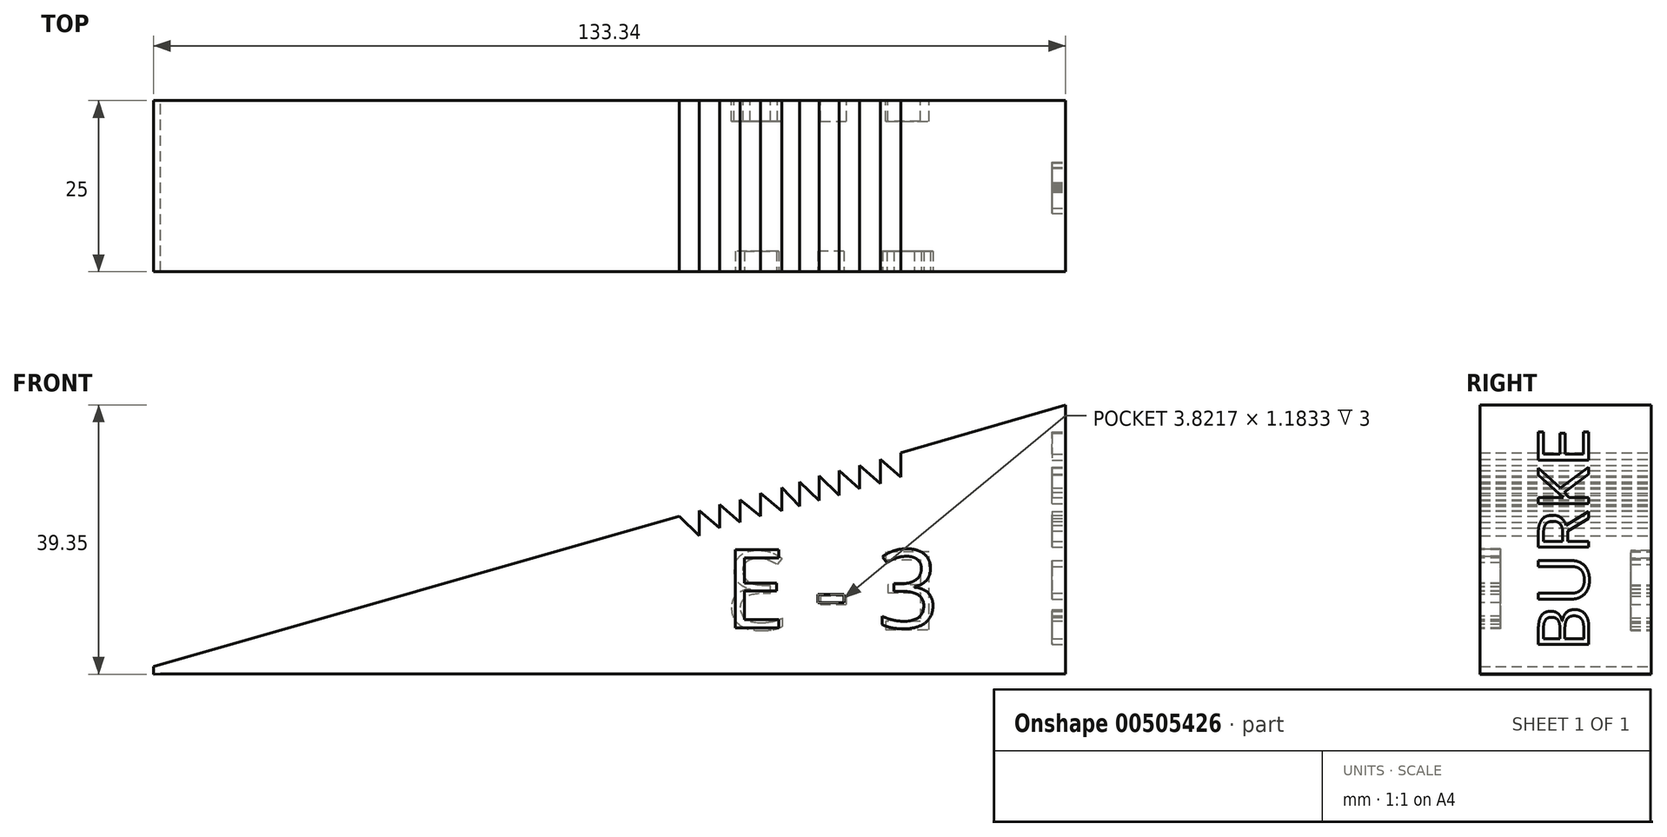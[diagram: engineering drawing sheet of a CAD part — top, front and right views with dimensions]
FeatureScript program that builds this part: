
annotation { "Feature Type Name" : "Feature", "Feature Type Description" : "" }
export const myFeature = defineFeature(function(context is Context, id is Id, definition is map)
    precondition{}
    {
        {
            var Q0;
            Q0=qCreatedBy(makeId("Front.planeOp"),FACE);
            var sketch = newSketch(context, id + "F0", { "sketchPlane" : qUnion([Q0])});
            skLineSegment(sketch, "E0", {"start": v(-57.96, -21.36) * mm, "end": v(74.33, -21.36) * mm});
            skLineSegment(sketch, "E1", {"start": v(74.33, -21.36) * mm, "end": v(74.33, 17.97) * mm});
            skLineSegment(sketch, "E2", {"start": v(74.33, 17.97) * mm, "end": v(50.24, 11) * mm});
            skLineSegment(sketch, "E3", {"start": v(50.24, 11) * mm, "end": v(50.24, 7.43) * mm});
            skLineSegment(sketch, "E4", {"start": v(50.24, 7.43) * mm, "end": v(47.23, 10.07) * mm});
            skLineSegment(sketch, "E5", {"start": v(47.23, 10.07) * mm, "end": v(47.23, 6.5) * mm});
            skLineSegment(sketch, "E6", {"start": v(47.23, 6.5) * mm, "end": v(44.22, 9.13) * mm});
            skLineSegment(sketch, "E7", {"start": v(44.22, 9.13) * mm, "end": v(44.22, 5.74) * mm});
            skLineSegment(sketch, "E8", {"start": v(44.22, 5.74) * mm, "end": v(41.2, 8.37) * mm});
            skLineSegment(sketch, "E9", {"start": v(41.2, 8.37) * mm, "end": v(41.2, 4.8) * mm});
            skLineSegment(sketch, "E10", {"start": v(41.2, 4.8) * mm, "end": v(38.28, 7.6) * mm});
            skLineSegment(sketch, "E11", {"start": v(38.28, 7.6) * mm, "end": v(38.28, 4) * mm});
            skLineSegment(sketch, "E12", {"start": v(38.28, 4) * mm, "end": v(35.43, 6.76) * mm});
            skLineSegment(sketch, "E13", {"start": v(35.43, 6.76) * mm, "end": v(35.43, 3.16) * mm});
            skLineSegment(sketch, "E14", {"start": v(35.43, 3.16) * mm, "end": v(32.83, 5.92) * mm});
            skLineSegment(sketch, "E15", {"start": v(32.83, 5.92) * mm, "end": v(32.83, 2.49) * mm});
            skLineSegment(sketch, "E16", {"start": v(32.83, 2.49) * mm, "end": v(29.73, 5.08) * mm});
            skLineSegment(sketch, "E17", {"start": v(29.73, 5.08) * mm, "end": v(29.73, 1.73) * mm});
            skLineSegment(sketch, "E18", {"start": v(29.73, 1.73) * mm, "end": v(26.71, 4.16) * mm});
            skLineSegment(sketch, "E19", {"start": v(26.71, 4.16) * mm, "end": v(26.71, 0.8) * mm});
            skLineSegment(sketch, "E20", {"start": v(26.71, 0.8) * mm, "end": v(23.78, 3.4) * mm});
            skLineSegment(sketch, "E21", {"start": v(23.78, 3.4) * mm, "end": v(23.78, 0) * mm});
            skLineSegment(sketch, "E22", {"start": v(23.78, 0) * mm, "end": v(20.76, 2.57) * mm});
            skLineSegment(sketch, "E23", {"start": v(20.76, 2.57) * mm, "end": v(20.76, -1.12) * mm});
            skLineSegment(sketch, "E24", {"start": v(20.76, -1.12) * mm, "end": v(17.83, 1.73) * mm});
            skLineSegment(sketch, "E25", {"start": v(17.83, 1.73) * mm, "end": v(-59.01, -20.26) * mm});
            skLineSegment(sketch, "E26", {"start": v(-59.01, -20.26) * mm, "end": v(-59.01, -21.38) * mm});
            skLineSegment(sketch, "E27", {"start": v(-59.01, -21.38) * mm, "end": v(-57.96, -21.36) * mm});
            skSolve(sketch);
        }
        {
            var Q0;
            Q0=makeQuery(id+"F0.imprint","IMPRINT",FACE,{"disambiguationData":[TD([[makeQuery(id+"F0.imprint","IMPRINT",EDGE,{"derivedFrom":sQuery(id+"F0.wireOp",EDGE,"E0")}),1.0]])]});
            extrude(context, id + "F1", {"entities" : qUnion([Q0]), "depth" : 25 * mm});
        }
        {
            var Q0;
            Q0=makeQuery(id+"F1.opExtrude","CAP_FACE",FACE,{"disambiguationData":[OSD([sQuery(id+"F0.wireOp",EDGE,"E0"),sQuery(id+"F0.wireOp",EDGE,"E1"),sQuery(id+"F0.wireOp",EDGE,"E2"),sQuery(id+"F0.wireOp",EDGE,"E3"),sQuery(id+"F0.wireOp",EDGE,"E4"),sQuery(id+"F0.wireOp",EDGE,"E5"),sQuery(id+"F0.wireOp",EDGE,"E6"),sQuery(id+"F0.wireOp",EDGE,"E7"),sQuery(id+"F0.wireOp",EDGE,"E8"),sQuery(id+"F0.wireOp",EDGE,"E9"),sQuery(id+"F0.wireOp",EDGE,"E10"),sQuery(id+"F0.wireOp",EDGE,"E11"),sQuery(id+"F0.wireOp",EDGE,"E12"),sQuery(id+"F0.wireOp",EDGE,"E13"),sQuery(id+"F0.wireOp",EDGE,"E14"),sQuery(id+"F0.wireOp",EDGE,"E15"),sQuery(id+"F0.wireOp",EDGE,"E16"),sQuery(id+"F0.wireOp",EDGE,"E17"),sQuery(id+"F0.wireOp",EDGE,"E18"),sQuery(id+"F0.wireOp",EDGE,"E19"),sQuery(id+"F0.wireOp",EDGE,"E20"),sQuery(id+"F0.wireOp",EDGE,"E21"),sQuery(id+"F0.wireOp",EDGE,"E22"),sQuery(id+"F0.wireOp",EDGE,"E23"),sQuery(id+"F0.wireOp",EDGE,"E24"),sQuery(id+"F0.wireOp",EDGE,"E25"),sQuery(id+"F0.wireOp",EDGE,"E26"),sQuery(id+"F0.wireOp",EDGE,"E27")])],"isStart":false});
            var sketch = newSketch(context, id + "F2", { "sketchPlane" : qUnion([Q0])});
            skText(sketch, "E28", { "text": "E - 3", "fontName": "OpenSans-Regular.ttf"});
            const initialGuessF2  = {"E28": [0.02446, -0.01458, 1, 0, 0.01148]};
            skSetInitialGuess(sketch, initialGuessF2);
            skSolve(sketch);
        }
        {
            var Q0;
            Q0=makeQuery(id+"F1.opExtrude","CAP_FACE",FACE,{"disambiguationData":[OSD([sQuery(id+"F0.wireOp",EDGE,"E0"),sQuery(id+"F0.wireOp",EDGE,"E1"),sQuery(id+"F0.wireOp",EDGE,"E2"),sQuery(id+"F0.wireOp",EDGE,"E3"),sQuery(id+"F0.wireOp",EDGE,"E4"),sQuery(id+"F0.wireOp",EDGE,"E5"),sQuery(id+"F0.wireOp",EDGE,"E6"),sQuery(id+"F0.wireOp",EDGE,"E7"),sQuery(id+"F0.wireOp",EDGE,"E8"),sQuery(id+"F0.wireOp",EDGE,"E9"),sQuery(id+"F0.wireOp",EDGE,"E10"),sQuery(id+"F0.wireOp",EDGE,"E11"),sQuery(id+"F0.wireOp",EDGE,"E12"),sQuery(id+"F0.wireOp",EDGE,"E13"),sQuery(id+"F0.wireOp",EDGE,"E14"),sQuery(id+"F0.wireOp",EDGE,"E15"),sQuery(id+"F0.wireOp",EDGE,"E16"),sQuery(id+"F0.wireOp",EDGE,"E17"),sQuery(id+"F0.wireOp",EDGE,"E18"),sQuery(id+"F0.wireOp",EDGE,"E19"),sQuery(id+"F0.wireOp",EDGE,"E20"),sQuery(id+"F0.wireOp",EDGE,"E21"),sQuery(id+"F0.wireOp",EDGE,"E22"),sQuery(id+"F0.wireOp",EDGE,"E23"),sQuery(id+"F0.wireOp",EDGE,"E24"),sQuery(id+"F0.wireOp",EDGE,"E25"),sQuery(id+"F0.wireOp",EDGE,"E26"),sQuery(id+"F0.wireOp",EDGE,"E27")])],"isStart":true});
            var sketch = newSketch(context, id + "F3", { "sketchPlane" : qUnion([Q0])});
            skText(sketch, "E29", { "text": "E - 3", "fontName": "OpenSans-Regular.ttf"});
            const initialGuessF3  = {"E29": [-0.05595, -0.01485, 1, 0, 0.01148]};
            skSetInitialGuess(sketch, initialGuessF3);
            skSolve(sketch);
        }
        {
            var Q0;
            Q0=qSketchRegion(id+"F2",true);
            extrude(context, id + "F4", {"entities" : qUnion([Q0]), "operationType" : NewBodyOperationType.REMOVE, "oppositeDirection" : true, "depth" : 3 * mm});
        }
        {
            var Q0;
            Q0=qSketchRegion(id+"F3",true);
            extrude(context, id + "F5", {"entities" : qUnion([Q0]), "operationType" : NewBodyOperationType.REMOVE, "oppositeDirection" : true, "depth" : 3 * mm});
        }
        {
            var Q0;
            Q0=makeQuery(id+"F1.opExtrude","SWEPT_FACE",FACE,{"disambiguationData":[OSD([sQuery(id+"F0.wireOp",EDGE,"E1")])]});
            var sketch = newSketch(context, id + "F6", { "sketchPlane" : qUnion([Q0])});
            skText(sketch, "E30", { "text": "BURKE", "fontName": "OpenSans-Regular.ttf"});
            const initialGuessF6  = {"E30": [-0.00911, -0.01804, 0, 1, 0.00744]};
            skSetInitialGuess(sketch, initialGuessF6);
            skSolve(sketch);
        }
        {
            var Q0;
            Q0=qSketchRegion(id+"F6",true);
            extrude(context, id + "F7", {"entities" : qUnion([Q0]), "operationType" : NewBodyOperationType.REMOVE, "oppositeDirection" : true, "depth" : 2 * mm});
        }
    });
